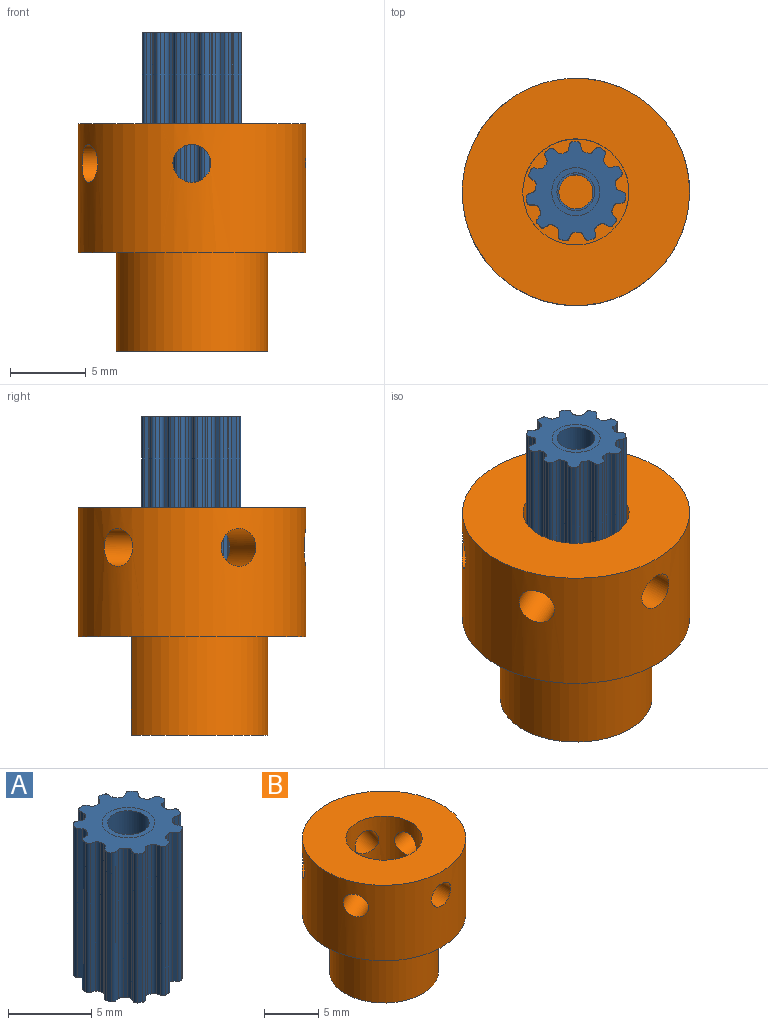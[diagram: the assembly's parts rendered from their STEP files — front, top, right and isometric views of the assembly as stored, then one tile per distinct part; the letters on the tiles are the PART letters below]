
ASSEMBLY  parts=2 mates=1
PART A: 94 faces, bbox 6.6x6.5x11 mm
  f0: cylinder r=1.12mm len=7.3mm, axis (0,0,-1), area 51.6mm2, adj f89,f93
  f1: cylinder r=0.23mm len=11mm, axis (0,0,1), area 3.3mm2, adj f2,f88,f89,f90
  f2: plane 11x0.3mm, normal (-1,-0.08,0), area 3.3mm2, adj f1,f3,f89,f90
  f3: cylinder r=0.3mm len=11mm, axis (0,0,1), area 3.6mm2, adj f2,f4,f89,f90
  f4: plane 11x0.2mm, normal (-0.54,0.84,0), area 2.7mm2, adj f3,f5,f89,f90
  f5: cylinder r=0.3mm len=11mm, axis (0,0,1), area 3.6mm2, adj f4,f6,f89,f90
  f6: plane 11x0.26mm, normal (0.49,0.87,0), area 3.3mm2, adj f5,f7,f89,f90
  f7: cylinder r=0.23mm len=11mm, axis (0,0,1), area 3.3mm2, adj f6,f8,f89,f90
  f8: cylinder r=3.3mm len=11mm, axis (0,0,-1), area 3.3mm2, adj f7,f9,f89,f90
  f9: cylinder r=0.23mm len=11mm, axis (0,0,1), area 3.3mm2, adj f8,f10,f89,f90
  f10: plane 11x0.24mm, normal (-0.79,-0.61,0), area 3.3mm2, adj f9,f11,f89,f90
  f11: cylinder r=0.3mm len=11mm, axis (0,0,1), area 3.6mm2, adj f10,f12,f89,f90
  f12: plane 11x0.22mm, normal (-0.91,0.42,0), area 2.7mm2, adj f11,f13,f89,f90
  f13: cylinder r=0.3mm len=11mm, axis (0,0,1), area 3.6mm2, adj f12,f14,f89,f90
  f14: plane 11x0.3mm, normal (-0.06,1,0), area 3.3mm2, adj f13,f15,f89,f90
  f15: cylinder r=0.23mm len=11mm, axis (0,0,1), area 3.3mm2, adj f14,f16,f89,f90
  f16: cylinder r=3.3mm len=11mm, axis (0,0,-1), area 3.3mm2, adj f15,f17,f89,f90
  f17: cylinder r=0.23mm len=11mm, axis (0,0,1), area 3.3mm2, adj f16,f18,f89,f90
  f18: plane 11x0.28mm, normal (-0.34,-0.94,0), area 3.3mm2, adj f17,f19,f89,f90
  f19: cylinder r=0.3mm len=11mm, axis (0,0,1), area 3.6mm2, adj f18,f20,f89,f90
  f20: plane 11x0.24mm, normal (-0.99,-0.14,0), area 2.7mm2, adj f19,f21,f89,f90
  f21: cylinder r=0.3mm len=11mm, axis (0,0,1), area 3.6mm2, adj f20,f22,f89,f90
  f22: plane 11x0.24mm, normal (-0.59,0.81,0), area 3.3mm2, adj f21,f23,f89,f90
  f23: cylinder r=0.23mm len=11mm, axis (0,0,1), area 3.3mm2, adj f22,f24,f89,f90
  f24: cylinder r=3.3mm len=11mm, axis (0,0,-1), area 3.3mm2, adj f23,f25,f89,f90
  f25: cylinder r=0.23mm len=11mm, axis (0,0,1), area 3.3mm2, adj f24,f26,f89,f90
  f26: plane 11x0.29mm, normal (0.22,-0.97,0), area 3.3mm2, adj f25,f27,f89,f90
  f27: cylinder r=0.3mm len=11mm, axis (0,0,1), area 3.6mm2, adj f26,f28,f89,f90
  f28: plane 11x0.18mm, normal (-0.76,-0.65,0), area 2.7mm2, adj f27,f29,f89,f90
  f29: cylinder r=0.3mm len=11mm, axis (0,0,1), area 3.6mm2, adj f28,f30,f89,f90
  f30: plane 11x0.28mm, normal (-0.93,0.36,0), area 3.3mm2, adj f29,f31,f89,f90
  f31: cylinder r=0.23mm len=11mm, axis (0,0,1), area 3.3mm2, adj f30,f32,f89,f90
  f32: cylinder r=3.3mm len=11mm, axis (0,0,-1), area 3.3mm2, adj f31,f33,f89,f90
  f33: cylinder r=0.23mm len=11mm, axis (0,0,1), area 3.3mm2, adj f32,f34,f89,f90
  f34: plane 11x0.21mm, normal (0.71,-0.7,0), area 3.3mm2, adj f33,f35,f89,f90
  f35: cylinder r=0.3mm len=11mm, axis (0,0,1), area 3.6mm2, adj f34,f36,f89,f90
  f36: plane 11x0.23mm, normal (-0.28,-0.96,0), area 2.7mm2, adj f35,f37,f89,f90
  f37: cylinder r=0.3mm len=11mm, axis (0,0,1), area 3.6mm2, adj f36,f38,f89,f90
  f38: plane 11x0.29mm, normal (-0.98,-0.2,0), area 3.3mm2, adj f37,f39,f89,f90
  f39: cylinder r=0.23mm len=11mm, axis (0,0,1), area 3.3mm2, adj f38,f40,f89,f90
  f40: cylinder r=3.3mm len=11mm, axis (0,0,-1), area 3.3mm2, adj f39,f41,f89,f90
  f41: cylinder r=0.23mm len=11mm, axis (0,0,1), area 3.3mm2, adj f40,f42,f89,f90
  f42: plane 11x0.29mm, normal (0.98,-0.2,0), area 3.3mm2, adj f41,f43,f89,f90
  f43: cylinder r=0.3mm len=11mm, axis (0,0,1), area 3.6mm2, adj f42,f44,f89,f90
  f44: plane 11x0.23mm, normal (0.28,-0.96,0), area 2.7mm2, adj f43,f45,f89,f90
  f45: cylinder r=0.3mm len=11mm, axis (0,0,1), area 3.6mm2, adj f44,f46,f89,f90
  f46: plane 11x0.21mm, normal (-0.71,-0.7,0), area 3.3mm2, adj f45,f47,f89,f90
  f47: cylinder r=0.23mm len=11mm, axis (0,0,1), area 3.3mm2, adj f46,f48,f89,f90
  f48: cylinder r=3.3mm len=11mm, axis (0,0,-1), area 3.3mm2, adj f47,f49,f89,f90
  f49: cylinder r=0.23mm len=11mm, axis (0,0,1), area 3.3mm2, adj f48,f50,f89,f90
  f50: plane 11x0.28mm, normal (0.93,0.36,0), area 3.3mm2, adj f49,f51,f89,f90
  f51: cylinder r=0.3mm len=11mm, axis (0,0,1), area 3.6mm2, adj f50,f52,f89,f90
  f52: plane 11x0.18mm, normal (0.76,-0.65,0), area 2.7mm2, adj f51,f53,f89,f90
  f53: cylinder r=0.3mm len=11mm, axis (0,0,1), area 3.6mm2, adj f52,f54,f89,f90
  f54: plane 11x0.29mm, normal (-0.22,-0.97,0), area 3.3mm2, adj f53,f55,f89,f90
  f55: cylinder r=0.23mm len=11mm, axis (0,0,1), area 3.3mm2, adj f54,f56,f89,f90
  f56: cylinder r=3.3mm len=11mm, axis (0,0,-1), area 3.3mm2, adj f55,f57,f89,f90
  f57: cylinder r=0.23mm len=11mm, axis (0,0,1), area 3.3mm2, adj f56,f58,f89,f90
  f58: plane 11x0.24mm, normal (0.59,0.81,0), area 3.3mm2, adj f57,f59,f89,f90
  f59: cylinder r=0.3mm len=11mm, axis (0,0,1), area 3.6mm2, adj f58,f60,f89,f90
  f60: plane 11x0.24mm, normal (0.99,-0.14,0), area 2.7mm2, adj f59,f61,f89,f90
  f61: cylinder r=0.3mm len=11mm, axis (0,0,1), area 3.6mm2, adj f60,f62,f89,f90
  f62: plane 11x0.28mm, normal (0.34,-0.94,0), area 3.3mm2, adj f61,f63,f89,f90
  f63: cylinder r=0.23mm len=11mm, axis (0,0,1), area 3.3mm2, adj f62,f64,f89,f90
  f64: cylinder r=3.3mm len=11mm, axis (0,0,-1), area 3.3mm2, adj f63,f65,f89,f90
  f65: cylinder r=0.23mm len=11mm, axis (0,0,1), area 3.3mm2, adj f64,f66,f89,f90
  f66: plane 11x0.3mm, normal (0.06,1,0), area 3.3mm2, adj f65,f67,f89,f90
  f67: cylinder r=0.3mm len=11mm, axis (0,0,1), area 3.6mm2, adj f66,f68,f89,f90
  f68: plane 11x0.22mm, normal (0.91,0.42,0), area 2.7mm2, adj f67,f69,f89,f90
  f69: cylinder r=0.3mm len=11mm, axis (0,0,1), area 3.6mm2, adj f68,f70,f89,f90
  f70: plane 11x0.24mm, normal (0.79,-0.61,0), area 3.3mm2, adj f69,f71,f89,f90
  f71: cylinder r=0.23mm len=11mm, axis (0,0,1), area 3.3mm2, adj f70,f72,f89,f90
  f72: cylinder r=3.3mm len=11mm, axis (0,0,-1), area 3.3mm2, adj f71,f73,f89,f90
  f73: cylinder r=0.23mm len=11mm, axis (0,0,1), area 3.3mm2, adj f72,f74,f89,f90
  f74: plane 11x0.26mm, normal (-0.49,0.87,0), area 3.3mm2, adj f73,f75,f89,f90
  f75: cylinder r=0.3mm len=11mm, axis (0,0,1), area 3.6mm2, adj f74,f76,f89,f90
  f76: plane 11x0.2mm, normal (0.54,0.84,0), area 2.7mm2, adj f75,f77,f89,f90
  f77: cylinder r=0.3mm len=11mm, axis (0,0,1), area 3.6mm2, adj f76,f78,f89,f90
  f78: plane 11x0.3mm, normal (1,-0.08,0), area 3.3mm2, adj f77,f79,f89,f90
  f79: cylinder r=0.23mm len=11mm, axis (0,0,1), area 3.3mm2, adj f78,f80,f89,f90
  f80: cylinder r=3.3mm len=11mm, axis (0,0,-1), area 3.3mm2, adj f79,f81,f89,f90
  f81: cylinder r=0.23mm len=11mm, axis (0,0,1), area 3.3mm2, adj f80,f82,f89,f90
  f82: plane 11x0.26mm, normal (-0.88,0.47,0), area 3.3mm2, adj f81,f83,f89,f90
  f83: cylinder r=0.3mm len=11mm, axis (0,0,1), area 3.6mm2, adj f82,f84,f89,f90
  f84: plane 11x0.24mm, normal (0,1,0), area 2.7mm2, adj f83,f85,f89,f90
  f85: cylinder r=0.3mm len=11mm, axis (0,0,1), area 3.6mm2, adj f84,f86,f89,f90
  f86: plane 11x0.26mm, normal (0.88,0.47,0), area 3.3mm2, adj f85,f87,f89,f90
  f87: cylinder r=0.23mm len=11mm, axis (0,0,1), area 3.3mm2, adj f86,f88,f89,f90
  f88: cylinder r=3.3mm len=11mm, axis (0,0,-1), area 3.3mm2, adj f1,f87,f89,f90
  f89: plane 6.57x6.52mm, normal (0,0,-1), area 23.9mm2, adj f0,f1,f2,f3,f4,f5,f6,f7
  f90: plane 6.57x6.52mm, normal (0,0,1), area 20mm2, adj f1,f2,f3,f4,f5,f6,f7,f8
  f91: plane 3.18x3.18mm, normal (0,0,1), area 3mm2, adj f90,f92
  f92: cylinder r=1.25mm len=3.7mm, axis (0,0,1), area 29.1mm2, adj f91,f93
  f93: plane 2.5x2.5mm, normal (0,0,1), area 0.9mm2, adj f0,f92
PART B: 13 faces, bbox 15.1x15x15 mm
  f0: cylinder r=7.5mm len=15mm, axis (0,0,-1), area 375.9mm2, adj f5,f6,f8,f9,f10,f11,f12
  f1: cylinder r=3.5mm len=7mm, axis (0,0,1), area 85mm2, adj f6,f7,f8,f9,f10,f11,f12
  f2: cylinder r=5mm len=10mm, axis (0,0,-1), area 162.4mm2, adj f3,f4,f5
  f3: plane 10x9mm, normal (0,0,-1), area 74.5mm2, adj f2,f4
  f4: plane 6.5x6mm, normal (0,1,0), area 39mm2, adj f2,f3,f5
  f5: plane 15x15mm, normal (0,0,-1), area 102.3mm2, adj f0,f2,f4
  f6: plane 15x15mm, normal (0,0,1), area 138.2mm2, adj f0,f1
  f7: plane 7x7mm, normal (0,0,1), area 38.5mm2, adj f1
  f8: cylinder r=1.25mm len=4.23mm, axis (0,-1,0), area 31.9mm2, adj f0,f1
  f9: cylinder r=1.25mm len=4.89mm, axis (-0.91,-0.42,0), area 31.9mm2, adj f0,f1
  f10: cylinder r=1.25mm len=4.83mm, axis (-0.76,0.65,0), area 31.9mm2, adj f0,f1
  f11: cylinder r=1.25mm len=4.76mm, axis (0.28,0.96,0), area 31.9mm2, adj f0,f1
  f12: cylinder r=1.25mm len=4.54mm, axis (0.99,0.14,0), area 31.9mm2, adj f0,f1
PLACE A rot(axis=(0,0,-1),15.2deg) t=(10.57,5.38,0.98)mm
PLACE B t=(10.57,5.38,-15.53)mm
MATE cylindrical B.f1 <-> A.f0  axis (0,0,1) through (10.57,5.38,-5.53)mm
